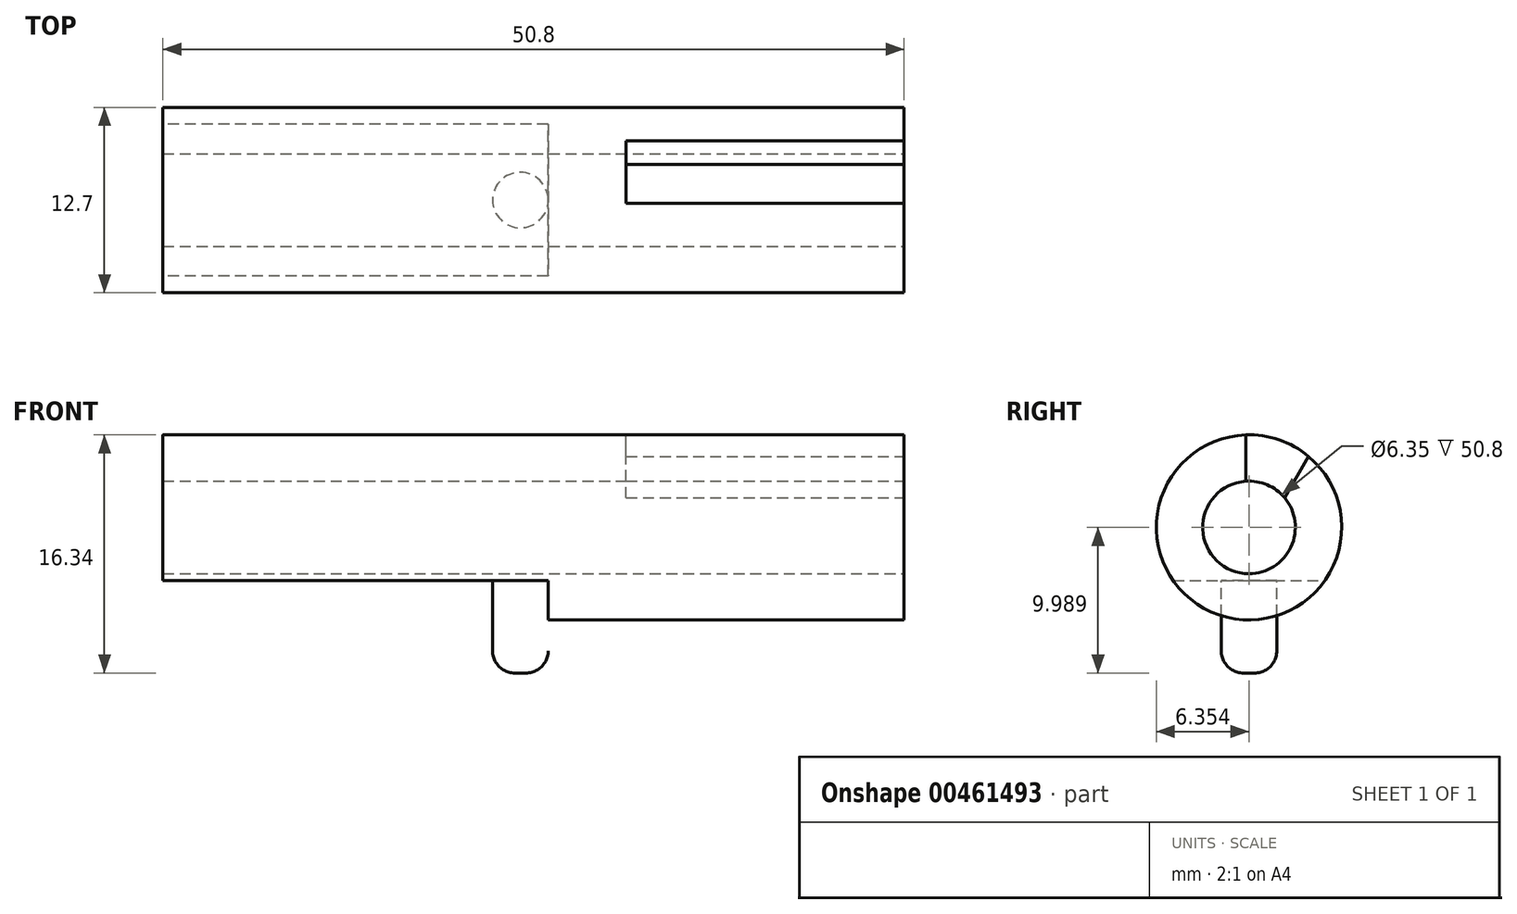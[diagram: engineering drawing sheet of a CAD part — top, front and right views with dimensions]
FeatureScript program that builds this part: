
annotation { "Feature Type Name" : "Feature", "Feature Type Description" : "" }
export const myFeature = defineFeature(function(context is Context, id is Id, definition is map)
    precondition{}
    {
        {
            var Q0;
            Q0=qCreatedBy(makeId("Right.planeOp"),FACE);
            var sketch = newSketch(context, id + "F0", { "sketchPlane" : qUnion([Q0])});
            skCircle(sketch, "E0", {"center": v(-34.12, 29.04) * mm, "radius": 6.35 * mm});
            skSolve(sketch);
        }
        {
            var Q0;
            Q0=makeQuery(id+"F0.imprint","IMPRINT",FACE,{"disambiguationData":[TD([[makeQuery(id+"F0.imprint","IMPRINT",EDGE,{"derivedFrom":sQuery(id+"F0.wireOp",EDGE,"E0")}),1.0]])]});
            extrude(context, id + "F1", {"entities" : qUnion([Q0]), "depth" : 50.8 * mm});
        }
        {
            var Q0;
            Q0=makeQuery(id+"F1.opExtrude","CAP_FACE",FACE,{"disambiguationData":[OSD([sQuery(id+"F0.wireOp",EDGE,"E0")])],"isStart":false});
            var sketch = newSketch(context, id + "F2", { "sketchPlane" : qUnion([Q0])});
            skCircle(sketch, "E1", {"center": v(-34.12, 29.04) * mm, "radius": 3.18 * mm});
            skSolve(sketch);
        }
        {
            var Q0;
            Q0=makeQuery(id+"F2.imprint","IMPRINT",FACE,{"disambiguationData":[TD([[makeQuery(id+"F2.imprint","IMPRINT",EDGE,{"derivedFrom":sQuery(id+"F2.wireOp",EDGE,"E1")}),1.0]])]});
            extrude(context, id + "F3", {"entities" : qUnion([Q0]), "operationType" : NewBodyOperationType.REMOVE, "oppositeDirection" : true, "depth" : 50.8 * mm});
        }
        {
            var Q0;
            Q0=makeQuery(id+"F1.opExtrude","CAP_FACE",FACE,{"disambiguationData":[OSD([sQuery(id+"F0.wireOp",EDGE,"E0")])],"isStart":false});
            var sketch = newSketch(context, id + "F4", { "sketchPlane" : qUnion([Q0])});
            skLineSegment(sketch, "E2", {"start": v(-34.33, 32.2) * mm, "end": v(-34.33, 35.39) * mm});
            skLineSegment(sketch, "E3", {"start": v(-31.68, 31.07) * mm, "end": v(-30.05, 33.92) * mm});
            skSolve(sketch);
        }
        {
            var Q0;
            {var subQ0=sQuery(id+"F4.wireOp",EDGE,"E2");Q0=makeQuery(id+"F4.imprint","IMPRINT",FACE,{"disambiguationData":[TD([[makeQuery(id+"F4.imprint","IMPRINT",EDGE,{"derivedFrom":subQ0}),-1.0]])]});}
            extrude(context, id + "F5", {"entities" : qUnion([Q0]), "operationType" : NewBodyOperationType.REMOVE, "oppositeDirection" : true, "depth" : 25.4 * mm});
        }
        {
            var Q0;
            Q0=makeQuery(id+"F5.boolean.opBoolean","COPY",FACE,{"derivedFrom":makeQuery(id+"F5.opExtrude","CAP_FACE",FACE,{"disambiguationData":[OSD([sQuery(id+"F0.wireOp",EDGE,"E0"),sQuery(id+"F2.wireOp",EDGE,"E1"),sQuery(id+"F4.wireOp",EDGE,"E2"),sQuery(id+"F4.wireOp",EDGE,"E3")])],"isStart":false})});
            extrude(context, id + "F6", {"entities" : qUnion([Q0]), "operationType" : NewBodyOperationType.ADD, "depth" : 6.35 * mm});
        }
        {
            var Q0;
            Q0=qCreatedBy(makeId("Top.planeOp"),FACE);
            var sketch = newSketch(context, id + "F7", { "sketchPlane" : qUnion([Q0])});
            skLineSegment(sketch, "E4", {"start": v(26.4, -26.4) * mm, "end": v(26.4, -40.61) * mm});
            skLineSegment(sketch, "E5", {"start": v(26.4, -40.61) * mm, "end": v(17.26, -40.61) * mm});
            skLineSegment(sketch, "E6", {"start": v(17.26, -40.61) * mm, "end": v(17.26, -26.2) * mm});
            skLineSegment(sketch, "E7", {"start": v(17.26, -26.2) * mm, "end": v(26.4, -26.4) * mm});
            skLineSegment(sketch, "E8", {"start": v(17.26, -40.61) * mm, "end": v(3.22, -40.61) * mm});
            skLineSegment(sketch, "E9", {"start": v(3.22, -40.61) * mm, "end": v(0, -40.61) * mm});
            skLineSegment(sketch, "E10", {"start": v(0, -40.61) * mm, "end": v(0, -23.69) * mm});
            skLineSegment(sketch, "E11", {"start": v(17.26, -26.2) * mm, "end": v(0, -25.81) * mm});
            skSolve(sketch);
        }
        {
            var Q0;
            Q0=makeQuery(id+"F7.imprint","IMPRINT",FACE,{"disambiguationData":[TD([[makeQuery(id+"F7.imprint","IMPRINT",EDGE,{"derivedFrom":sQuery(id+"F7.wireOp",EDGE,"E4")}),-1.0]])]});
            var Q1;
            Q1=makeQuery(id+"F7.imprint","IMPRINT",FACE,{"disambiguationData":[TD([[makeQuery(id+"F7.imprint","IMPRINT",EDGE,{"derivedFrom":sQuery(id+"F7.wireOp",EDGE,"E6")}),1.0]])]});
            extrude(context, id + "F8", {"entities" : qUnion([Q0, Q1]), "operationType" : NewBodyOperationType.REMOVE, "depth" : 25.4 * mm});
        }
        {
            var Q0;
            Q0=makeQuery(id+"F8.boolean.opBoolean","COPY",FACE,{"derivedFrom":makeQuery(id+"F8.opExtrude","CAP_FACE",FACE,{"disambiguationData":[OSD([sQuery(id+"F7.wireOp",EDGE,"E4"),sQuery(id+"F7.wireOp",EDGE,"E5"),sQuery(id+"F7.wireOp",EDGE,"E7"),sQuery(id+"F7.wireOp",EDGE,"E8"),sQuery(id+"F7.wireOp",EDGE,"E9"),sQuery(id+"F7.wireOp",EDGE,"E10"),sQuery(id+"F7.wireOp",EDGE,"E11")])],"isStart":false})});
            var sketch = newSketch(context, id + "F9", { "sketchPlane" : qUnion([Q0])});
            skCircle(sketch, "E12", {"center": v(24.5, 34.12) * mm, "radius": 1.9 * mm});
            skPoint(sketch, "E12.centerSnap0", {"position": v(0, 34.12) * mm});
            skSolve(sketch);
        }
        {
            var Q0;
            Q0=makeQuery(id+"F9.imprint","IMPRINT",FACE,{"disambiguationData":[TD([[makeQuery(id+"F9.imprint","IMPRINT",EDGE,{"derivedFrom":sQuery(id+"F9.wireOp",EDGE,"E12")}),1.0]])]});
            extrude(context, id + "F10", {"entities" : qUnion([Q0]), "depth" : 6.35 * mm});
        }
        {
            var Q0;
            Q0=makeQuery(id+"F10.opExtrude","CAP_EDGE",EDGE,{"disambiguationData":[OSD([sQuery(id+"F9.wireOp",EDGE,"E12")])],"isStart":false});
            fillet(context, id + "F11", {"entities" : qUnion([Q0]), "radius" : 1.52 * mm, "tangentPropagation" : true, "allowEdgeOverflow" : false});
        }
    });
